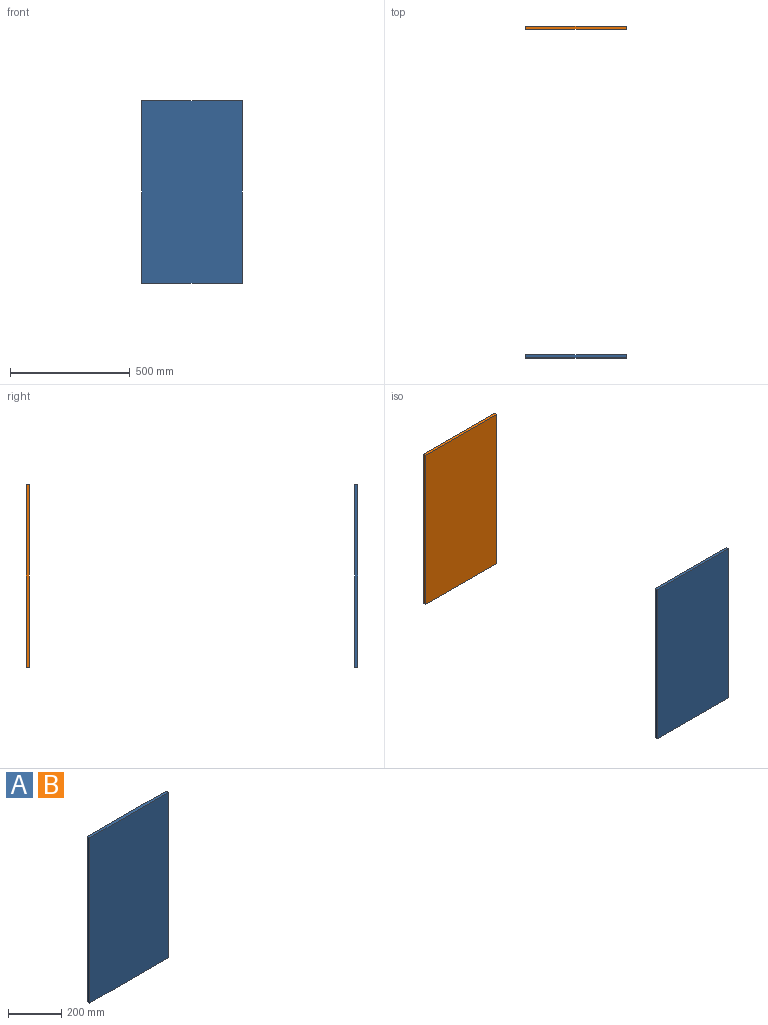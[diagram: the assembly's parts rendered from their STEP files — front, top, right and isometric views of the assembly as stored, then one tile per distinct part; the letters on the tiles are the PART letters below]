
ASSEMBLY  parts=2 mates=1
PART A: 6 faces, bbox 419.1x12.7x762 mm
  f0: plane 419.1x12.7mm, normal (0,0,1), area 5322.6mm2, adj f1,f3,f4,f5
  f1: plane 762x12.7mm, normal (-1,0,0), area 9677.4mm2, adj f0,f2,f4,f5
  f2: plane 419.1x12.7mm, normal (0,0,-1), area 5322.6mm2, adj f1,f3,f4,f5
  f3: plane 762x12.7mm, normal (1,0,0), area 9677.4mm2, adj f0,f2,f4,f5
  f4: plane 762x419.1mm, normal (0,-1,0), area 319354.2mm2, adj f0,f1,f2,f3
  f5: plane 762x419.1mm, normal (0,1,0), area 319354.2mm2, adj f0,f1,f2,f3
PART B: same geometry as A
PLACE A t=(-175.96,-41.4,80.75)mm fixed
PLACE B t=(-175.96,1330.2,80.75)mm
MATE parallel B.f0 <-> A.f0  axis (0,0,1) through (-175.96,1323.85,461.75)mm
